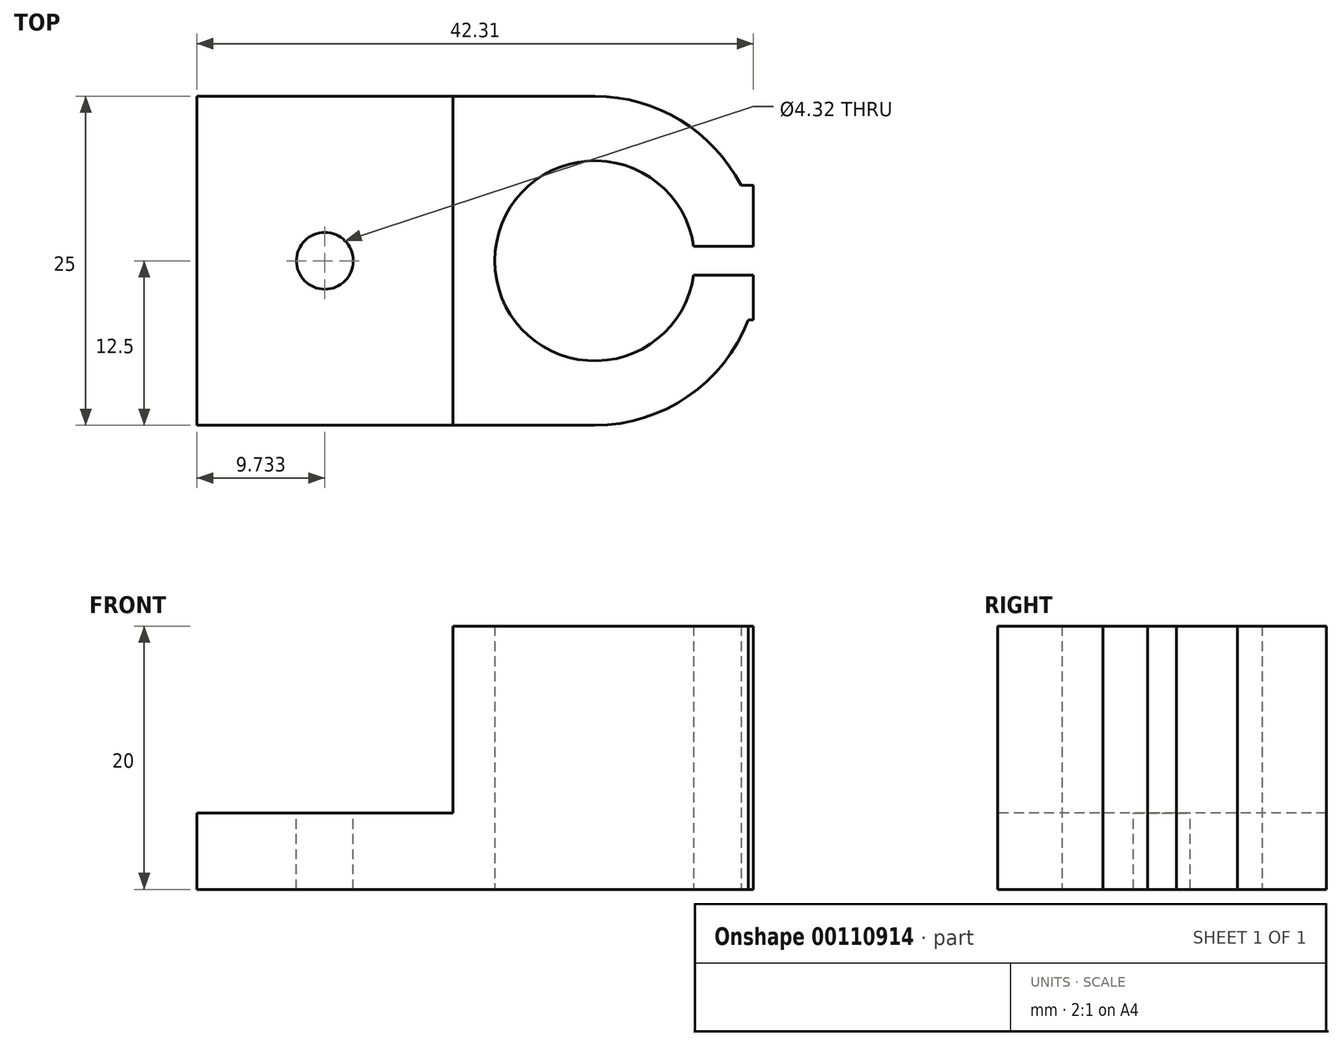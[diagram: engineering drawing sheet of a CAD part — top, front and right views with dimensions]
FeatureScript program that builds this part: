
annotation { "Feature Type Name" : "Feature", "Feature Type Description" : "" }
export const myFeature = defineFeature(function(context is Context, id is Id, definition is map)
    precondition{}
    {
        {
            var Q0;
            Q0=qCreatedBy(makeId("Top.planeOp"),FACE);
            var sketch = newSketch(context, id + "F0", { "sketchPlane" : qUnion([Q0])});
            skArc(sketch, "E0", {"start": v(7.52, 1.1) * mm, "mid": v(-7.6, 0) * mm, "end": v(7.52, -1.1) * mm});
            skArc(sketch, "E1", {"start": v(0, -12.5) * mm, "mid": v(7.07, -10.3) * mm, "end": v(11.66, -4.5) * mm});
            skLineSegment(sketch, "E2.left", {"start": v(-48.25, 4.5) * mm, "end": v(-48.25, -4.5) * mm, "construction": true});
            skLineSegment(sketch, "E2.right", {"start": v(-10.79, 4.5) * mm, "end": v(-10.79, -4.5) * mm, "construction": true});
            skLineSegment(sketch, "E3", {"start": v(0, 0) * mm, "end": v(-10.79, 0) * mm, "construction": true});
            skLineSegment(sketch, "E4", {"start": v(0, 12.5) * mm, "end": v(-30.25, 12.5) * mm});
            skLineSegment(sketch, "E5", {"start": v(-30.25, 12.5) * mm, "end": v(-30.25, -4.5) * mm});
            skPoint(sketch, "E5.endSnap0", {"position": v(-29.52, -4.5) * mm});
            skLineSegment(sketch, "E6", {"start": v(-10.79, 4.5) * mm, "end": v(-10.79, -4.5) * mm});
            skLineSegment(sketch, "E7", {"start": v(-30.25, -4.5) * mm, "end": v(-30.25, -12.5) * mm});
            skLineSegment(sketch, "E8", {"start": v(-30.25, -12.5) * mm, "end": v(0, -12.5) * mm});
            skLineSegment(sketch, "E9", {"start": v(11.11, 5.73) * mm, "end": v(12.06, 5.73) * mm});
            skLineSegment(sketch, "E10", {"start": v(12.06, 5.73) * mm, "end": v(12.06, 1.1) * mm});
            skLineSegment(sketch, "E11", {"start": v(12.06, 1.1) * mm, "end": v(7.52, 1.1) * mm});
            skLineSegment(sketch, "E12", {"start": v(7.52, -1.1) * mm, "end": v(12.06, -1.1) * mm});
            skLineSegment(sketch, "E13", {"start": v(12.06, -1.1) * mm, "end": v(12.06, -4.5) * mm});
            skLineSegment(sketch, "E14", {"start": v(12.06, -4.5) * mm, "end": v(11.66, -4.5) * mm});
            skArc(sketch, "E15.trimOffspring", {"start": v(11.11, 5.73) * mm, "mid": v(6.5, 10.67) * mm, "end": v(0, 12.5) * mm});
            skLineSegment(sketch, "E16", {"start": v(-10.79, 4.5) * mm, "end": v(-10.79, 12.5) * mm});
            skLineSegment(sketch, "E17", {"start": v(-10.79, -4.5) * mm, "end": v(-10.79, -12.5) * mm});
            skSolve(sketch);
        }
        {
            var Q0;
            Q0=makeQuery(id+"F0.imprint","IMPRINT",FACE,{"disambiguationData":[TD([[makeQuery(id+"F0.imprint","IMPRINT",EDGE,{"derivedFrom":sQuery(id+"F0.wireOp",EDGE,"E0")}),-1.0]])]});
            extrude(context, id + "F1", {"entities" : qUnion([Q0]), "depth" : 20 * mm});
        }
        {
            var Q0;
            {var subQ0=sQuery(id+"F0.wireOp",EDGE,"E5");Q0=makeQuery(id+"F0.imprint","IMPRINT",FACE,{"disambiguationData":[TD([[makeQuery(id+"F0.imprint","IMPRINT",EDGE,{"derivedFrom":subQ0}),1.0]])]});}
            var Q1;
            Q1=makeQuery(id+"F0.imprint","IMPRINT",FACE,{"disambiguationData":[TD([[makeQuery(id+"F0.imprint","IMPRINT",EDGE,{"derivedFrom":sQuery(id+"F0.wireOp",EDGE,"9WJQLeq8-gHu1-3Nqd-rDEh-Rfgkn3N6eF2B")}),1.0]])]});
            extrude(context, id + "F2", {"entities" : qUnion([Q0, Q1]), "operationType" : NewBodyOperationType.ADD, "depth" : 5.8 * mm});
        }
        {
            var Q0;
            Q0=makeQuery(id+"F2.opExtrude","CAP_FACE",FACE,{"disambiguationData":[OSD([sQuery(id+"F0.wireOp",EDGE,"E4"),sQuery(id+"F0.wireOp",EDGE,"E5"),sQuery(id+"F0.wireOp",EDGE,"E6"),sQuery(id+"F0.wireOp",EDGE,"E7"),sQuery(id+"F0.wireOp",EDGE,"E8"),sQuery(id+"F0.wireOp",EDGE,"E16"),sQuery(id+"F0.wireOp",EDGE,"E17")])],"isStart":false});
            var sketch = newSketch(context, id + "F3", { "sketchPlane" : qUnion([Q0])});
            skCircle(sketch, "E18", {"center": v(-20.52, 0) * mm, "radius": 2.16 * mm});
            skPoint(sketch, "E18.centerSnap0", {"position": v(-20.52, 12.5) * mm});
            skPoint(sketch, "E18.centerSnap1", {"position": v(-30.25, 0) * mm});
            skSolve(sketch);
        }
        {
            var Q0;
            Q0 = qSketchRegion(id + "F3", true);
            extrude(context, id + "F4", {"entities" : qUnion([Q0]), "operationType" : NewBodyOperationType.REMOVE, "oppositeDirection" : true, "depth" : 25 * mm});
        }
    });
